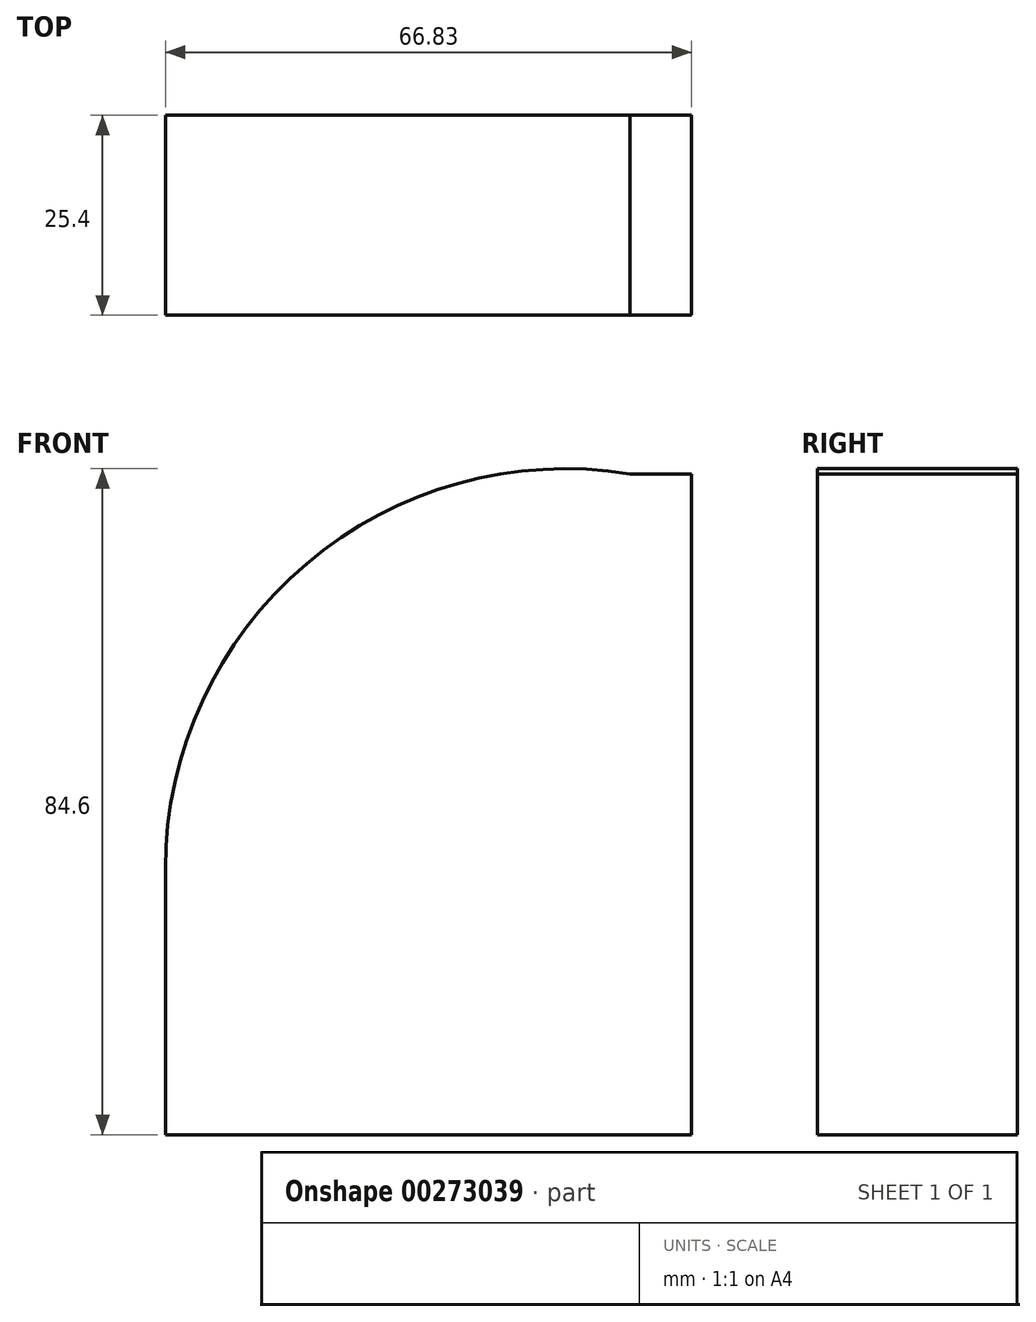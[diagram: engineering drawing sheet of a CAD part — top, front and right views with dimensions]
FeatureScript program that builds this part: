
annotation { "Feature Type Name" : "Feature", "Feature Type Description" : "" }
export const myFeature = defineFeature(function(context is Context, id is Id, definition is map)
    precondition{}
    {
        {
            var Q0;
            Q0=qCreatedBy(makeId("Front.planeOp"),FACE);
            var sketch = newSketch(context, id + "F0", { "sketchPlane" : qUnion([Q0])});
            skLineSegment(sketch, "E0.bottom", {"start": v(0, 0) * mm, "end": v(-7.85, 0) * mm});
            skLineSegment(sketch, "E0.top", {"start": v(0, 83.94) * mm, "end": v(-7.85, 83.94) * mm});
            skLineSegment(sketch, "E0.left", {"start": v(0, 0) * mm, "end": v(0, 83.94) * mm});
            skLineSegment(sketch, "E0.right", {"start": v(-7.85, 0) * mm, "end": v(-7.85, 83.94) * mm});
            skLineSegment(sketch, "E1.bottom", {"start": v(-7.85, 0) * mm, "end": v(-66.83, 0) * mm});
            skLineSegment(sketch, "E1.top", {"start": v(-7.85, 33.8) * mm, "end": v(-66.83, 33.8) * mm});
            skLineSegment(sketch, "E1.left", {"start": v(-7.85, 0) * mm, "end": v(-7.85, 33.8) * mm});
            skLineSegment(sketch, "E1.right", {"start": v(-66.83, 0) * mm, "end": v(-66.83, 33.8) * mm});
            skArc(sketch, "E2", {"start": v(-7.85, 83.94) * mm, "mid": v(-48.93, 72.5) * mm, "end": v(-66.83, 33.8) * mm});
            skSolve(sketch);
        }
        {
            var Q0;
            Q0 = qSketchRegion(id + "F0", true);
            extrude(context, id + "F1", {"entities" : qUnion([Q0]), "depth" : 25.4 * mm});
        }
    });
